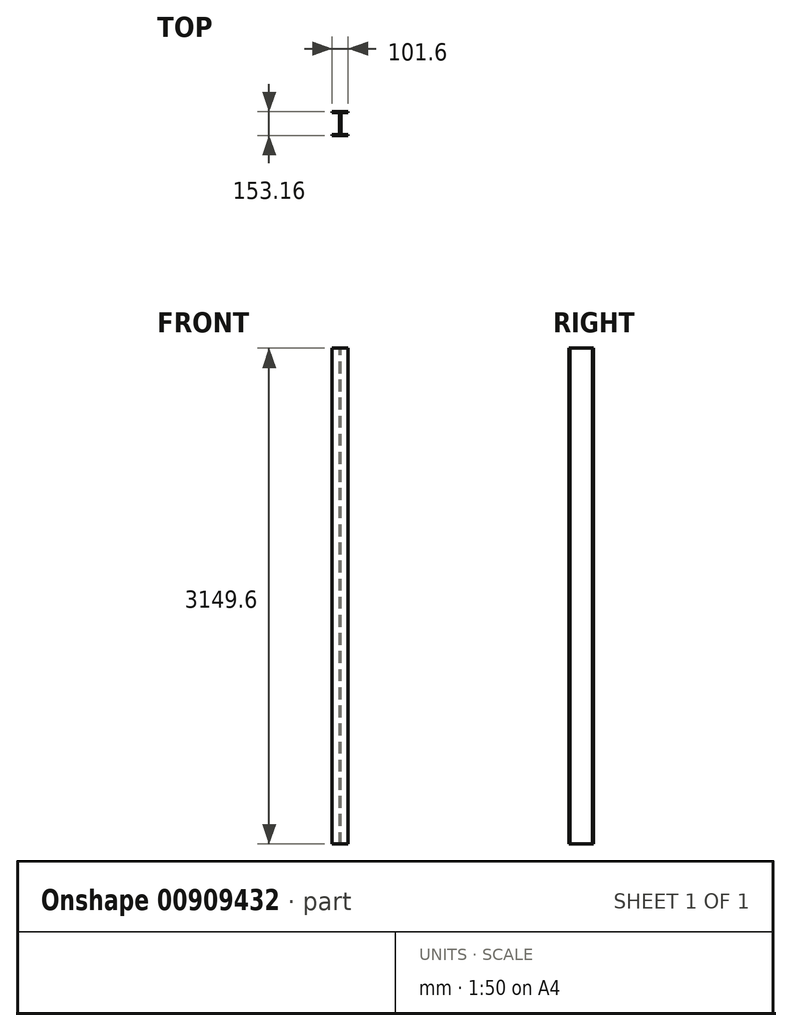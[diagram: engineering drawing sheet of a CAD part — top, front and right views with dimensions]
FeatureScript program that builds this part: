
annotation { "Feature Type Name" : "Feature", "Feature Type Description" : "" }
export const myFeature = defineFeature(function(context is Context, id is Id, definition is map)
    precondition{}
    {
        {
            var Q0;
            Q0=qCreatedBy(makeId("Top.planeOp"),FACE);
            var sketch = newSketch(context, id + "F0", { "sketchPlane" : qUnion([Q0])});
            skLineSegment(sketch, "E0.bottom", {"start": v(-50.8, 76.58) * mm, "end": v(50.8, 76.58) * mm});
            skLineSegment(sketch, "E0.top", {"start": v(-50.8, -76.58) * mm, "end": v(50.8, -76.58) * mm});
            skLineSegment(sketch, "E0.left", {"start": v(-50.8, 76.58) * mm, "end": v(-50.8, -76.58) * mm});
            skLineSegment(sketch, "E0.right", {"start": v(50.8, 76.58) * mm, "end": v(50.8, -76.58) * mm});
            skLineSegment(sketch, "E1", {"start": v(-50.8, 0) * mm, "end": v(0, 0) * mm, "construction": true});
            skLineSegment(sketch, "E2", {"start": v(0, 0) * mm, "end": v(0, 76.58) * mm, "construction": true});
            skSolve(sketch);
        }
        {
            var Q0;
            Q0 = qSketchRegion(id + "F0", true);
            extrude(context, id + "F1", {"entities" : qUnion([Q0]), "endBound" : BoundingType.SYMMETRIC, "depth" : 3149.6 * mm, "offsetDistance" : 25.4 * mm});
        }
        {
            var Q0;
            Q0=makeQuery(id+"F1.opExtrude","CAP_FACE",FACE,{"disambiguationData":[OSD([sQuery(id+"F0.wireOp",EDGE,"E0.bottom"),sQuery(id+"F0.wireOp",EDGE,"E0.top"),sQuery(id+"F0.wireOp",EDGE,"E0.left"),sQuery(id+"F0.wireOp",EDGE,"E0.right")])],"isStart":false});
            var sketch = newSketch(context, id + "F2", { "sketchPlane" : qUnion([Q0])});
            skLineSegment(sketch, "E3.bottom", {"start": v(50.8, 70.74) * mm, "end": v(3.56, 70.74) * mm});
            skLineSegment(sketch, "E3.top", {"start": v(50.8, -70.74) * mm, "end": v(3.56, -70.74) * mm});
            skLineSegment(sketch, "E3.left", {"start": v(50.8, 70.74) * mm, "end": v(50.8, -70.74) * mm});
            skLineSegment(sketch, "E3.right", {"start": v(3.56, 70.74) * mm, "end": v(3.56, -70.74) * mm});
            skLineSegment(sketch, "E4", {"start": v(0, 0) * mm, "end": v(3.56, 0) * mm, "construction": true});
            skLineSegment(sketch, "E5", {"start": v(0, 0) * mm, "end": v(-3.56, 0) * mm, "construction": true});
            skLineSegment(sketch, "E6.MirrorCS", {"start": v(-3.56, 70.74) * mm, "end": v(-3.56, -70.74) * mm});
            skLineSegment(sketch, "E7.MirrorCS", {"start": v(-50.8, 70.74) * mm, "end": v(-3.56, 70.74) * mm});
            skLineSegment(sketch, "E8.MirrorCS", {"start": v(-50.8, 70.74) * mm, "end": v(-50.8, -70.74) * mm});
            skLineSegment(sketch, "E9.MirrorCS", {"start": v(-50.8, -70.74) * mm, "end": v(-3.56, -70.74) * mm});
            skSolve(sketch);
        }
        {
            var Q0;
            Q0 = qSketchRegion(id + "F2", true);
            extrude(context, id + "F3", {"entities" : qUnion([Q0]), "operationType" : NewBodyOperationType.REMOVE, "endBound" : BoundingType.THROUGH_ALL, "oppositeDirection" : true, "depth" : 25.4 * mm, "offsetDistance" : 25.4 * mm});
        }
    });
